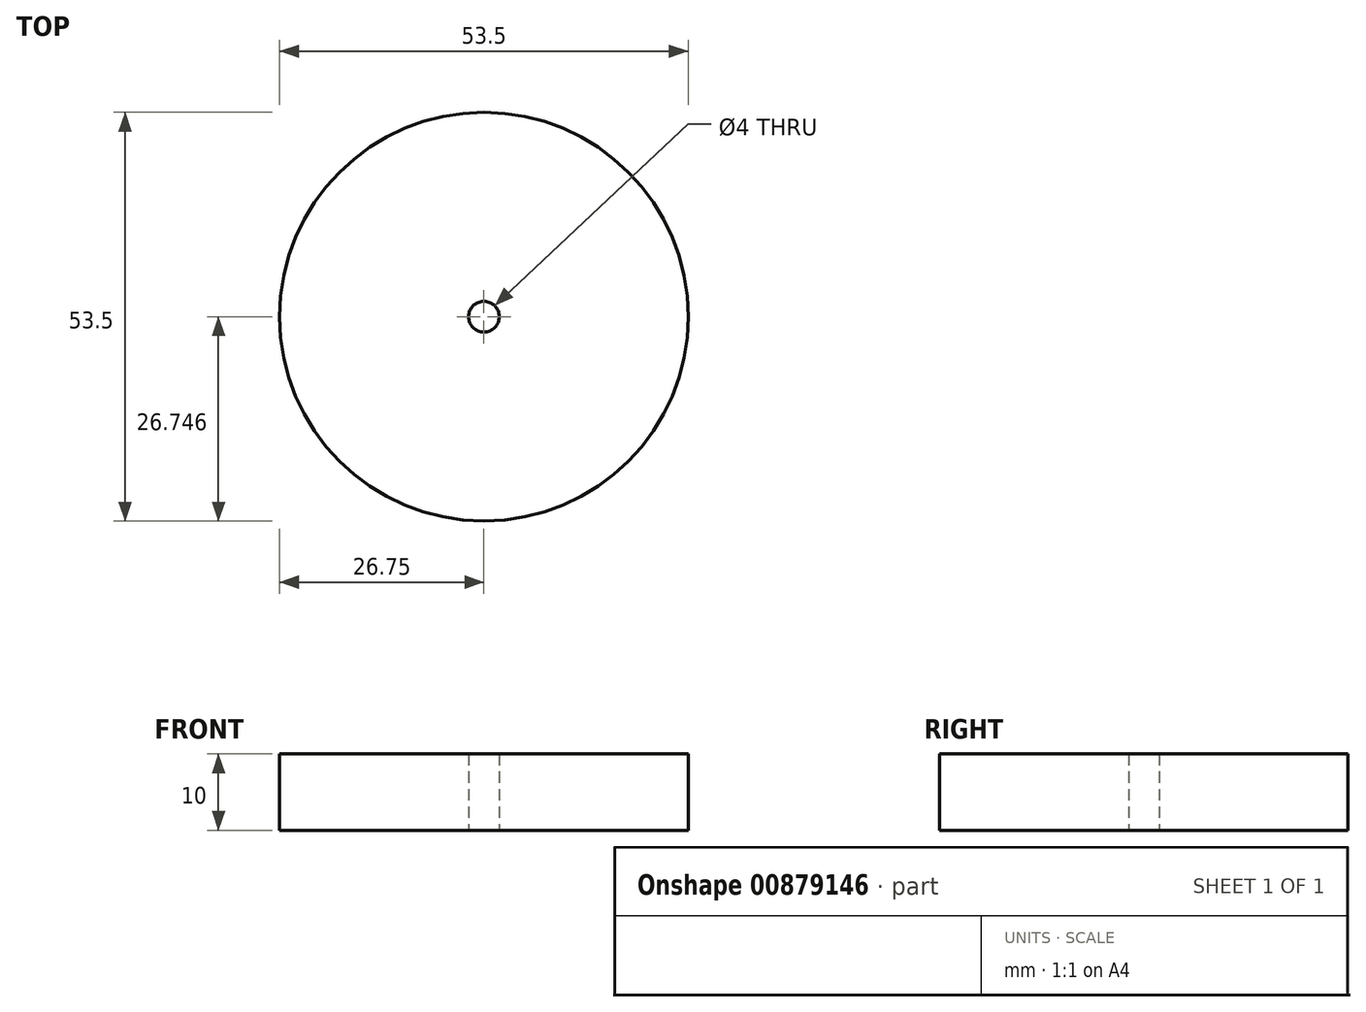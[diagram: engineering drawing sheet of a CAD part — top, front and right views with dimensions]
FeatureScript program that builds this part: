
annotation { "Feature Type Name" : "Feature", "Feature Type Description" : "" }
export const myFeature = defineFeature(function(context is Context, id is Id, definition is map)
    precondition{}
    {
        {
            var Q0;
            Q0=qCreatedBy(makeId("Top.planeOp"),FACE);
            var sketch = newSketch(context, id + "F0", { "sketchPlane" : qUnion([Q0])});
            skCircle(sketch, "E0", {"center": v(0, -1.42) * mm, "radius": 26.75 * mm});
            skCircle(sketch, "E1", {"center": v(0, -1.42) * mm, "radius": 2 * mm});
            skSolve(sketch);
        }
        {
            var Q0;
            Q0=makeQuery(id+"F0.imprint","IMPRINT",FACE,{"disambiguationData":[TD([[makeQuery(id+"F0.imprint","IMPRINT",EDGE,{"derivedFrom":sQuery(id+"F0.wireOp",EDGE,"E0")}),1.0]])]});
            extrude(context, id + "F1", {"entities" : qUnion([Q0]), "depth" : 10 * mm, "offsetDistance" : 25 * mm});
        }
    });
